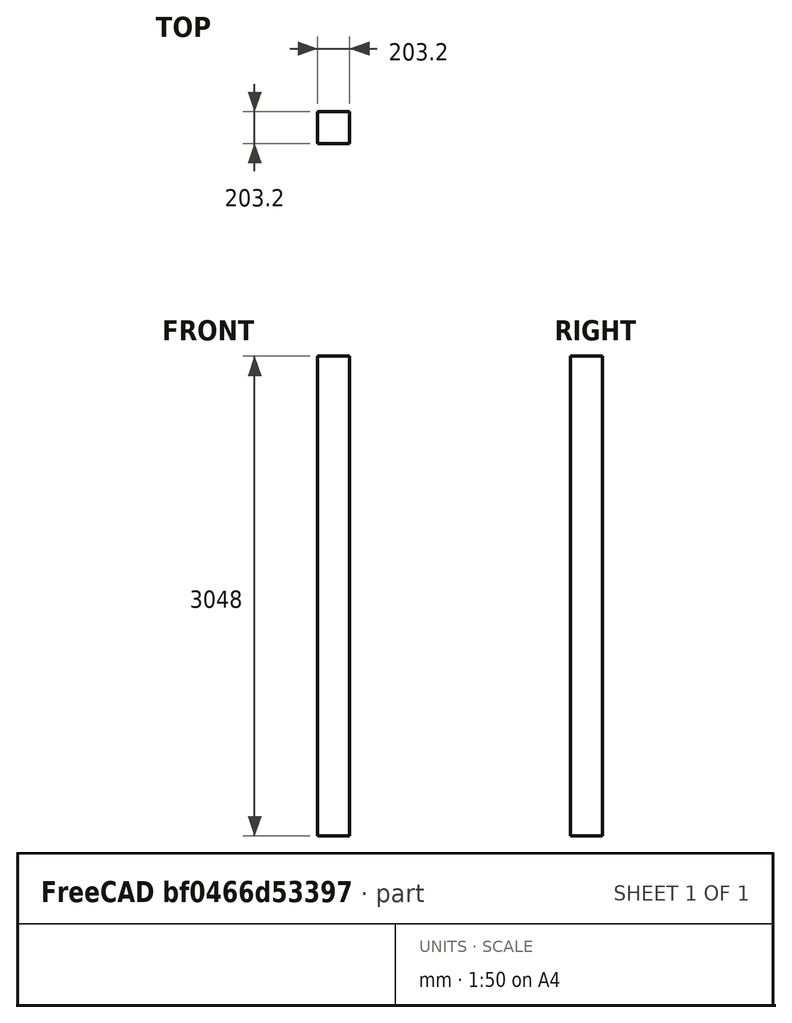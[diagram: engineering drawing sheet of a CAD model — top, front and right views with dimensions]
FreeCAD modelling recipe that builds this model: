
FCSTD DOCUMENT  (FreeCAD 0.20R29177 (Git))
Label: postTenFoot
License: All rights reserved
LicenseURL: http://en.wikipedia.org/wiki/All_rights_reserved
objects: Sketcher::SketchObject×1, PartDesign::Pad×1, PartDesign::Body×1
note: 4 computed .brp shape members not serialized (recipe doc carries the construction recipe); baked Part::Feature solids carry a one-line shape summary decoded from their .brp

FEATURE [Sketcher::SketchObject] Sketch
  FullyConstrained = true
  MapMode = 5
  Support = -> [XY_Plane]
  sketch-geometry (4):
    g0: LineSegment StartX=0 StartY=0 StartZ=0 EndX=203.2 EndY=0 EndZ=0
    g1: LineSegment StartX=203.2 StartY=0 StartZ=0 EndX=203.2 EndY=203.2 EndZ=0
    g2: LineSegment StartX=203.2 StartY=203.2 StartZ=0 EndX=0 EndY=203.2 EndZ=0
    g3: LineSegment StartX=0 StartY=203.2 StartZ=0 EndX=0 EndY=0 EndZ=0
  constraints (11):
    c: Coincident(g0,g1)
    c: Coincident(g1,g2)
    c: Coincident(g2,g3)
    c: Coincident(g3,g0)
    c: Horizontal(g0)
    c: Horizontal(g2)
    c: Vertical(g1)
    c: Vertical(g3)
    c: Coincident(g0,g-1)
    c: Equal(g3,g0)
    c: DistanceX(g0,g0) = 203.2
FEATURE [PartDesign::Pad] Pad
  Direction = (0,0,1)
  Length = 3048
  Length2 = 9.525
  Profile = -> Sketch
  ReferenceAxis = -> Sketch [N_Axis]
  Type = 0
FEATURE [PartDesign::Body] Body
  Group = -> [Sketch,Pad]
  Origin = -> Origin
  Tip = -> Pad
